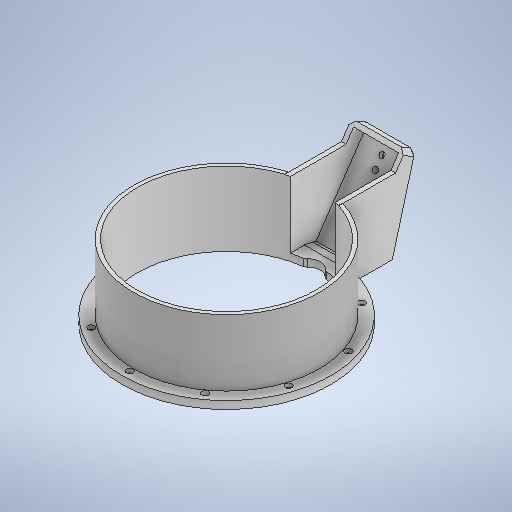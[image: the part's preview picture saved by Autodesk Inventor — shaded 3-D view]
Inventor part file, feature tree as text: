
AUTODESK INVENTOR PART (.ipt)
format: ipt  version: 2025.2 (Build 292293000, 293)  size: 1,539,584 bytes
history: native  units: in
note: dims shown in document units (in); Inventor stores cm internally (conversion verified against a paired STEP export)
features: extrude x33, sketch x33, plane x14, projected_geometry x6, chamfer x5, other x3
ambient origin geometry x8: Origin, YZ Plane, XZ Plane, XY Plane, X Axis, Y Axis, Z Axis, Center Point
bodies: Body1 (feature_tree)
feature tree (94):
  other  "Cylinder.ipt"
  extrude  "Extrusion1"  Depth=0.3937in
  extrude  "Extrusion2"  Depth=0.3937in TaperAngle=0.0deg
  sketch  "Sketch3"  dims[d7=11.2205in d8=10.6299in]
  extrude  "Extrusion3"  Depth=10.6299in
  extrude  "Extrusion5"  Depth=0.1969in TaperAngle=0.0deg
  sketch  "Sketch6"  dims[d24=0.1969in d25=0.0in d31=0.0in d32=0.0in]
  extrude  "Extrusion6"  Depth=10.6299in
  extrude  "Extrusion7"  TaperAngle=0.0deg  [1 undecoded]
  extrude  "Extrusion8"  Depth=9.8425in
  plane  "Work Plane1"
  extrude  "Extrusion9"  Depth=10.6299in
  extrude  "Extrusion21"  Depth=0.3937in
  sketch  "Sketch19"  dims[d107=2.2047in d108=0.0in d113=2.5591in]
  extrude  "Extrusion34"  Depth=2.5591in
  extrude  "Extrusion53"  Depth=0.5433in
  plane  "Work Plane2"
  plane  "Work Plane3"
  plane  "Work Plane5"
  plane  "Work Plane6"
  extrude  "Extrusion88"  Depth=0.0787in
  extrude  "Extrusion89"  Depth=0.0787in
  extrude  "Extrusion91"  TaperAngle=90.0deg  [1 undecoded]
  plane  "Work Plane7"
  plane  "Work Plane8"
  plane  "Work Plane9"
  plane  "Work Plane10"
  extrude  "Extrusion102"  Depth=0.0787in
  plane  "Work Plane11"
  plane  "Work Plane12"
  extrude  "Extrusion108"  Depth=0.3425in
  plane  "Work Plane13"
  extrude  "Extrusion113"  Depth=10.4151in
  plane  "Work Plane14"
  extrude  "Extrusion117"  Depth=0.5433in
  extrude  "Extrusion118"  Depth=3.5433in
  extrude  "Extrusion120"  Depth=2.7608in
  extrude  "Extrusion121"  [1 undecoded]
  extrude  "Extrusion122"  Depth=0.0591in
  extrude  "Extrusion128"  Depth=2.3622in
  chamfer  "Chamfer19"  Distance=1.1811in
  extrude  "Extrusion129"  Depth=3.3661in TaperAngle=0.0deg
  chamfer  "Chamfer20"  Distance=3.3465in
  extrude  "Extrusion130"  Depth=2.7559in TaperAngle=0.0deg
  chamfer  "Chamfer21"  Distance=2.7559in
  extrude  "Extrusion131"  Depth=0.7087in TaperAngle=0.0deg
  extrude  "Extrusion132"  Depth=0.2362in
  extrude  "Extrusion133"  Depth=3.3465in TaperAngle=0.0deg
  plane  "Work Plane15"
  extrude  "Extrusion135"  Depth=0.0197in TaperAngle=0.0deg
  extrude  "Extrusion136"  Depth=3.3465in TaperAngle=0.0deg
  chamfer  "Chamfer22"  Distance=0.7874in
  chamfer  "Chamfer23"  Distance=0.7874in
  extrude  "Extrusion137"  Depth=0.3937in TaperAngle=0.0deg
  extrude  "Extrusion138"  Depth=0.2362in
  extrude  "Extrusion139"  Depth=0.2362in TaperAngle=45.0deg
  other  "Solid12::Cylinder.ipt"
  other  "TaggingFeature1"
  sketch  "Sketch1"  dims[d0=0.3937in d2=10.2362in]
  sketch  "Sketch2"  dims[d3=0.0in d4=0.0in d5=0.3937in d6=0.0in]
  sketch  "Sketch5"  dims[d17=10.6299in d18=0.2953in]
  sketch  "Sketch7"  dims[d33=2.1654in d34=0.0in d35=9.8425in]
  sketch  "Sketch9"  dims[d36=10.6299in d46=9.065in]
  sketch  "Sketch14"  dims[d47=0.3937in d48=0.0in d88=0.0787in]
  sketch  "Sketch22"  dims[d117=0.0591in d120=0.5433in]
  sketch  "Sketch Circular Pattern3"  dims[d10=0.1969in d11=0.0in d15=0.1969in d16=0.0in]
  sketch  "Sketch76"  dims[d122=9.4488in d134=0.0787in]
  sketch  "Sketch77"  dims[d164=1.5298in d165=0.0787in]
  sketch  "Sketch79"  dims[d166=1.8325in d167=90.0deg]
  sketch  "Sketch93"  dims[d173=1.1614in d174=0.0in d175=0.0787in]
  sketch  "Sketch99"  dims[d209=0.2165in d210=0.3425in]
  sketch  "Sketch104"  dims[d211=3.937in d213=360.0deg d217=10.4151in]
  sketch  "Sketch108"  dims[d218=9.065in d223=0.5433in]
  sketch  "Sketch109"  dims[d224=1.8228in d225=3.5433in]
  sketch  "Sketch111"  dims[d226=2.564in d227=2.7608in]
  sketch  "Sketch112"  dims[d228=3.5433in d269=-3.5433in]
  sketch  "Sketch113"  dims[d306=4.5276in d307=0.0591in]
  projected_geometry  "Projected Loop4"
  projected_geometry  "Projected Loop5"
  sketch  "Sketch119"  dims[d308=2.7608in d309=2.3622in]
  projected_geometry  "Projected Loop9"
  sketch  "Sketch120"  dims[d313=3.3661in d314=0.3937in d315=0.0in d316=0.0in]
  projected_geometry  "Projected Loop10"
  projected_geometry  "Projected Loop11"
  sketch  "Sketch121"  dims[d452=0.1772in]
  sketch  "Sketch122"  dims[d453=0.3396in]
  sketch  "Sketch123"  dims[d454=0.1772in]
  sketch  "Sketch124"  dims[d455=0.3396in d489=1.1811in d490=0.0in]
  sketch  "Sketch126"  dims[d491=3.3661in d492=0.3937in d493=0.0in d494=0.0in d497=3.3661in d498=0.0in d548=3.3465in d549=0.0in]
  sketch  "Sketch127"  dims[d554=120.0deg d563=2.7559in d564=0.0in d579=2.7559in d580=0.0in]
  sketch  "Sketch130"  dims[d592=2.7559in d593=0.0in d600=0.7087in d601=0.0in]
  sketch  "Sketch131"  dims[d604=2.7559in d605=0.2362in]
  sketch  "Sketch132"  dims[d606=0.2362in d607=3.3465in d608=0.0in d609=0.7874in d610=0.0in d611=3.3465in d612=0.0in d626=0.7874in d627=0.7874in d629=0.3937in d630=0.0in d631=0.2362in d632=0.2362in d633=0.0787in d634=45.0deg d635=1.9685in d636=0.0in d637=0.2362in d638=0.0787in d639=45.0deg d640=1.1811in d641=0.3937in d642=0.0in d643=0.0787in d644=0.0787in d645=45.0deg d646=0.1575in d647=0.0in d648=3.5433in d649=0.0in d652=0.2756in d653=0.2756in d655=3.5433in d656=0.0in d661=-0.7874in d662=0.4724in d663=0.4724in d664=0.5906in d665=0.0in d666=0.4724in d667=0.3937in d668=0.0in d669=0.2323in d670=0.0787in d671=45.0deg d672=0.3268in d673=0.0787in d674=45.0deg d675=2.2835in d676=0.0in d677=2.2835in d678=0.0in d679=0.1683in d680=0.0in d143=0.0197in d144=0.0344in d145=0.0197in d146=0.0344in d153=0.0in d154=0.0in d155=0.0in d156=0.0in d201=0.0197in d202=0.0344in d203=0.0197in d204=0.0344in d215=0.0197in d216=0.0344in d294=0.0197in d295=0.0344in d296=0.0197in d297=0.0344in d330=0.0197in d331=0.0344in d332=0.0197in d333=0.0344in d419=0.0197in d420=0.0344in d421=0.0197in d422=0.0344in d423=0.0344in d424=0.0197in d425=0.0344in d505=0.0197in d506=0.0344in d507=0.0197in d508=0.0344in d514=0.0197in d515=0.0344in d516=0.0197in d517=0.0344in d546=0.0197in d547=0.0344in d555=0.0197in d556=0.0344in d557=0.0197in d558=0.0344in d588=0.0197in d589=0.0344in d590=0.0197in d591=0.0344in d617=0.0197in d618=0.0344in d619=0.0197in d620=0.0344in d628=0.0197in]
  projected_geometry  "Projected Loop15"
note: 3 required parameter values undecoded (feature->parameter linkage not recoverable at this tier; creation-order binding heuristic only, values carry confidence <= 0.55)
